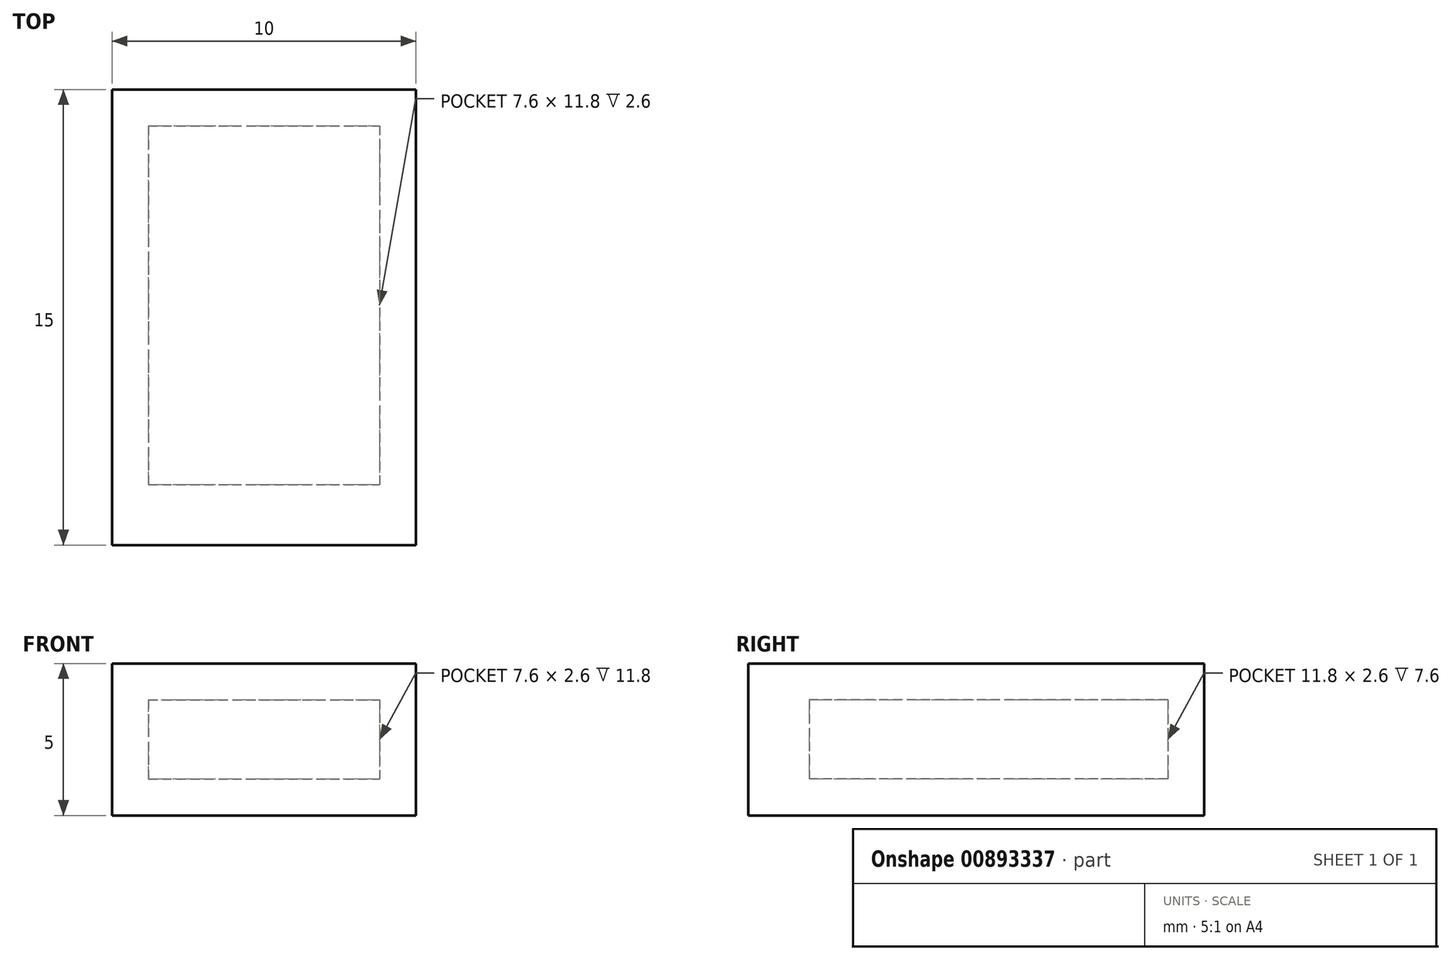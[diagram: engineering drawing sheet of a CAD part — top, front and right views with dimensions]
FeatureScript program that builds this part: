
annotation { "Feature Type Name" : "Feature", "Feature Type Description" : "" }
export const myFeature = defineFeature(function(context is Context, id is Id, definition is map)
    precondition{}
    {
        {
            var Q0;
            Q0=qCreatedBy(makeId("Top.planeOp"),FACE);
            var sketch = newSketch(context, id + "F0", { "sketchPlane" : qUnion([Q0])});
            skLineSegment(sketch, "E0.bottom", {"start": v(-2.99, 1) * mm, "end": v(7.01, 1) * mm});
            skLineSegment(sketch, "E0.top", {"start": v(-2.99, -12) * mm, "end": v(7.01, -12) * mm});
            skLineSegment(sketch, "E0.left", {"start": v(-2.99, 1) * mm, "end": v(-2.99, -12) * mm});
            skLineSegment(sketch, "E0.right", {"start": v(7.01, 1) * mm, "end": v(7.01, -12) * mm});
            skSolve(sketch);
        }
        {
            var Q0;
            Q0 = qSketchRegion(id + "F0", true);
            extrude(context, id + "F1", {"entities" : qUnion([Q0]), "depth" : 5 * mm, "offsetDistance" : 25 * mm});
        }
        {
            var Q0;
            Q0=makeQuery(id+"F1.opExtrude","SWEPT_FACE",FACE,{"disambiguationData":[OSD([sQuery(id+"F0.wireOp",EDGE,"E0.top")])]});
            shell(context, id + "F2", {"entities" : qUnion([Q0]), "thickness" : 1.2 * mm});
        }
        {
            var Q0;
            Q0=makeQuery(id+"F1.opExtrude","SWEPT_FACE",FACE,{"disambiguationData":[OSD([sQuery(id+"F0.wireOp",EDGE,"E0.top")])]});
            var sketch = newSketch(context, id + "F3", { "sketchPlane" : qUnion([Q0])});
            skLineSegment(sketch, "E1.bottom", {"start": v(-2.99, 5) * mm, "end": v(7.01, 5) * mm});
            skLineSegment(sketch, "E1.top", {"start": v(-2.99, 0) * mm, "end": v(7.01, 0) * mm});
            skLineSegment(sketch, "E1.left", {"start": v(-2.99, 5) * mm, "end": v(-2.99, 0) * mm});
            skLineSegment(sketch, "E1.right", {"start": v(7.01, 5) * mm, "end": v(7.01, 0) * mm});
            skSolve(sketch);
        }
        {
            var Q0;
            Q0 = qSketchRegion(id + "F3", true);
            extrude(context, id + "F4", {"entities" : qUnion([Q0]), "operationType" : NewBodyOperationType.ADD, "depth" : 2 * mm, "offsetDistance" : 25 * mm});
        }
    });
